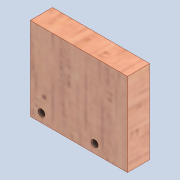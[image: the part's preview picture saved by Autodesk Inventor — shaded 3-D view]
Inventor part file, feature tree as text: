
AUTODESK INVENTOR PART (.ipt)
format: ipt  version: 2020 (Build 240168000, 168)  size: 153,600 bytes
history: native  units: mm
features: other x3, sketch x2, reference x2, extrude x1, hole x1
ambient origin geometry x8: Origin, YZ Plane, XZ Plane, XY Plane, X Axis, Y Axis, Z Axis, Center Point
bodies: Solid1 (feature_tree)
feature tree (9):
  extrude  "Extrusion1"  Depth=30.0mm
  hole  "Hole1"  [1 undecoded]
  sketch  "Sketch1"  dims[d0=35.0mm d1=30.0mm]
  sketch  "Sketch6"  dims[d2=8.0mm d3=0.0mm d37=2.459mm d38=8.0mm d39=4.0mm d40=2.0mm d41=90.0deg d42=8.8mm d43=20.594885mm]
  reference  "Reference1"
  reference  "Reference2"
  parser-record x1  (decoder bookkeeping rows leaked as tree rows — omitted from the tree; the rows remain in map.json)
  other  "0005-00-00 Ansamblu_General_V1.iam"
  other  "0005-20-1003 Switch:1"
note: 1 required parameter value undecoded (feature->parameter linkage not recoverable at this tier; creation-order binding heuristic only, values carry confidence <= 0.55)
note: 1 file-system path scrubbed to <path> (originals preserved in map.json)
